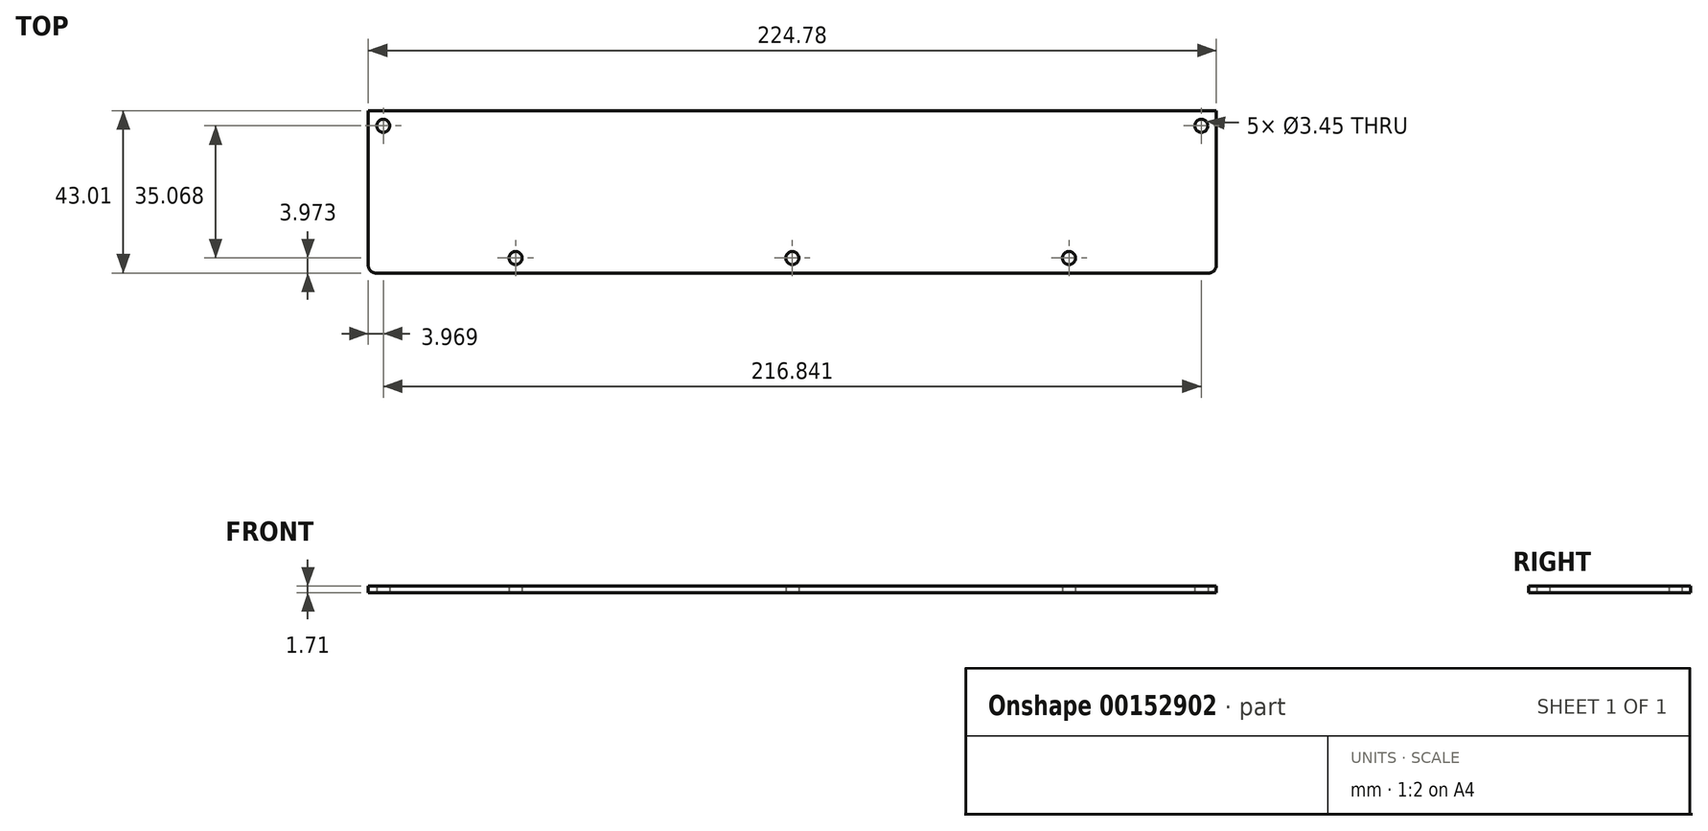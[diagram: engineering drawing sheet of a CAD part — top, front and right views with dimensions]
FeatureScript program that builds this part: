
annotation { "Feature Type Name" : "Feature", "Feature Type Description" : "" }
export const myFeature = defineFeature(function(context is Context, id is Id, definition is map)
    precondition{}
    {
        {
            var Q0;
            Q0=qCreatedBy(makeId("Top.planeOp"),FACE);
            var sketch = newSketch(context, id + "F0", { "sketchPlane" : qUnion([Q0])});
            skLineSegment(sketch, "E0.bottom", {"start": v(0, 0) * mm, "end": v(224.78, 0) * mm});
            skLineSegment(sketch, "E0.top", {"start": v(0, -43) * mm, "end": v(224.78, -43) * mm});
            skLineSegment(sketch, "E0.left", {"start": v(0, 0) * mm, "end": v(0, -43) * mm});
            skLineSegment(sketch, "E0.right", {"start": v(224.78, 0) * mm, "end": v(224.78, -43) * mm});
            skLineSegment(sketch, "E1", {"start": v(0, -3.97) * mm, "end": v(3.97, -3.97) * mm, "construction": true});
            skLineSegment(sketch, "E2", {"start": v(3.97, -3.97) * mm, "end": v(3.97, 0) * mm, "construction": true});
            skLineSegment(sketch, "E3", {"start": v(220.8, 0) * mm, "end": v(220.8, -3.97) * mm, "construction": true});
            skLineSegment(sketch, "E4", {"start": v(220.8, -3.97) * mm, "end": v(224.78, -3.97) * mm, "construction": true});
            skLineSegment(sketch, "E5", {"start": v(112.39, -43) * mm, "end": v(112.39, -39.04) * mm, "construction": true});
            skLineSegment(sketch, "E6", {"start": v(112.39, -39.04) * mm, "end": v(185.74, -39.04) * mm, "construction": true});
            skLineSegment(sketch, "E7", {"start": v(112.39, -39.04) * mm, "end": v(39.04, -39.04) * mm, "construction": true});
            skCircle(sketch, "E8", {"center": v(3.97, -3.97) * mm, "radius": 1.73 * mm});
            skCircle(sketch, "E9", {"center": v(39.04, -39.04) * mm, "radius": 1.73 * mm});
            skCircle(sketch, "E10", {"center": v(112.39, -39.04) * mm, "radius": 1.73 * mm});
            skCircle(sketch, "E11", {"center": v(185.74, -39.04) * mm, "radius": 1.73 * mm});
            skCircle(sketch, "E12", {"center": v(220.8, -3.97) * mm, "radius": 1.73 * mm});
            skLineSegment(sketch, "E13", {"start": v(185.74, -3.97) * mm, "end": v(185.74, -39.04) * mm, "construction": true});
            skLineSegment(sketch, "E14", {"start": v(185.74, -3.97) * mm, "end": v(220.8, -3.97) * mm, "construction": true});
            skLineSegment(sketch, "E15", {"start": v(220.8, -3.97) * mm, "end": v(220.8, -3.97) * mm});
            skSolve(sketch);
        }
        {
            var Q0;
            Q0 = qSketchRegion(id + "F0", true);
            extrude(context, id + "F1", {"entities" : qUnion([Q0]), "depth" : 1.7 * mm});
        }
        {
            var Q0;
            Q0=makeQuery(id+"F1.opExtrude","SWEPT_EDGE",EDGE,{"disambiguationData":[OSD([sQuery(id+"F0.wireOp",EDGE,"E0.top"),sQuery(id+"F0.wireOp",EDGE,"E0.left")])]});
            var Q1;
            Q1=makeQuery(id+"F1.opExtrude","SWEPT_EDGE",EDGE,{"disambiguationData":[OSD([sQuery(id+"F0.wireOp",EDGE,"E0.top"),sQuery(id+"F0.wireOp",EDGE,"E0.right")])]});
            fillet(context, id + "F2", {"entities" : qUnion([Q0, Q1]), "radius" : 1.98 * mm, "tangentPropagation" : true, "allowEdgeOverflow" : false});
        }
    });
